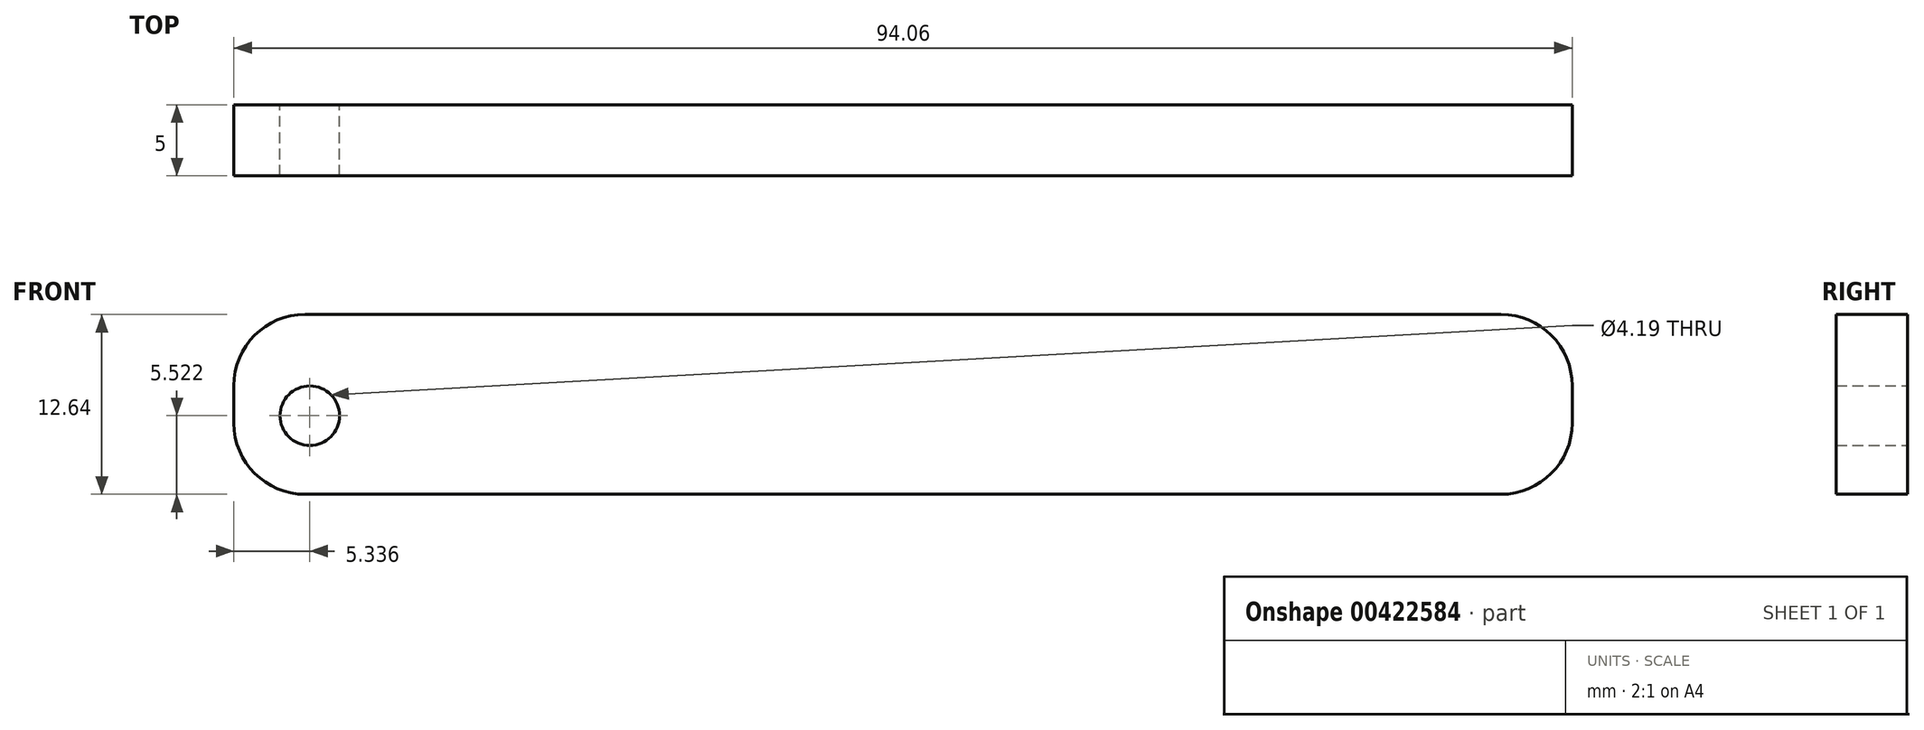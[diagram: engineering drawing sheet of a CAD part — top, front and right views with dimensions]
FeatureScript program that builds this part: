
annotation { "Feature Type Name" : "Feature", "Feature Type Description" : "" }
export const myFeature = defineFeature(function(context is Context, id is Id, definition is map)
    precondition{}
    {
        {
            var Q0;
            Q0=qCreatedBy(makeId("Front.planeOp"),FACE);
            var sketch = newSketch(context, id + "F0", { "sketchPlane" : qUnion([Q0])});
            skLineSegment(sketch, "E0.bottom", {"start": v(-57.01, 29.06) * mm, "end": v(37.05, 29.06) * mm});
            skLineSegment(sketch, "E0.top", {"start": v(-57.01, 16.42) * mm, "end": v(37.05, 16.42) * mm});
            skLineSegment(sketch, "E0.left", {"start": v(-57.01, 29.06) * mm, "end": v(-57.01, 16.42) * mm});
            skLineSegment(sketch, "E0.right", {"start": v(37.05, 29.06) * mm, "end": v(37.05, 16.42) * mm});
            skCircle(sketch, "E1", {"center": v(-51.67, 21.94) * mm, "radius": 2.1 * mm});
            skSolve(sketch);
        }
        {
            var Q0;
            Q0=makeQuery(id+"F0.imprint","IMPRINT",FACE,{"disambiguationData":[TD([[makeQuery(id+"F0.imprint","IMPRINT",EDGE,{"derivedFrom":sQuery(id+"F0.wireOp",EDGE,"E0.bottom")}),-1.0]])]});
            extrude(context, id + "F1", {"entities" : qUnion([Q0]), "depth" : 5 * mm});
        }
        {
            var Q0;
            Q0=makeQuery(id+"F1.opExtrude","SWEPT_EDGE",EDGE,{"disambiguationData":[OSD([sQuery(id+"F0.wireOp",EDGE,"E0.bottom"),sQuery(id+"F0.wireOp",EDGE,"E0.right")])]});
            var Q1;
            Q1=makeQuery(id+"F1.opExtrude","SWEPT_EDGE",EDGE,{"disambiguationData":[OSD([sQuery(id+"F0.wireOp",EDGE,"E0.top"),sQuery(id+"F0.wireOp",EDGE,"E0.right")])]});
            var Q2;
            Q2=makeQuery(id+"F1.opExtrude","SWEPT_EDGE",EDGE,{"disambiguationData":[OSD([sQuery(id+"F0.wireOp",EDGE,"E0.top"),sQuery(id+"F0.wireOp",EDGE,"E0.left")])]});
            var Q3;
            Q3=makeQuery(id+"F1.opExtrude","SWEPT_EDGE",EDGE,{"disambiguationData":[OSD([sQuery(id+"F0.wireOp",EDGE,"E0.bottom"),sQuery(id+"F0.wireOp",EDGE,"E0.left")])]});
            fillet(context, id + "F2", {"entities" : qUnion([Q0, Q1, Q2, Q3]), "radius" : 5 * mm, "tangentPropagation" : true, "allowEdgeOverflow" : false});
        }
        {
            var Q0;
            Q0=qCreatedBy(makeId("Front.planeOp"),FACE);
            var sketch = newSketch(context, id + "F3", { "sketchPlane" : qUnion([Q0])});
            skLineSegment(sketch, "E2.bottom", {"start": v(-59.9, 31.72) * mm, "end": v(-43.48, 31.72) * mm});
            skLineSegment(sketch, "E2.top", {"start": v(-59.9, 29.06) * mm, "end": v(-43.48, 29.06) * mm});
            skLineSegment(sketch, "E2.left", {"start": v(-59.9, 31.72) * mm, "end": v(-59.9, 29.06) * mm});
            skLineSegment(sketch, "E2.right", {"start": v(-43.48, 31.72) * mm, "end": v(-43.48, 29.06) * mm});
            skSolve(sketch);
        }
        {
            var Q0;
            Q0=sQuery(id+"F3.wireOp",EDGE,"E2.bottom");
            var Q1;
            Q1=sQuery(id+"F3.wireOp",EDGE,"E2.top");
            extrude(context, id + "F4", {"bodyType" : ToolBodyType.SURFACE, "surfaceEntities" : qUnion([Q0, Q1]), "depth" : 10 * mm});
        }
    });
